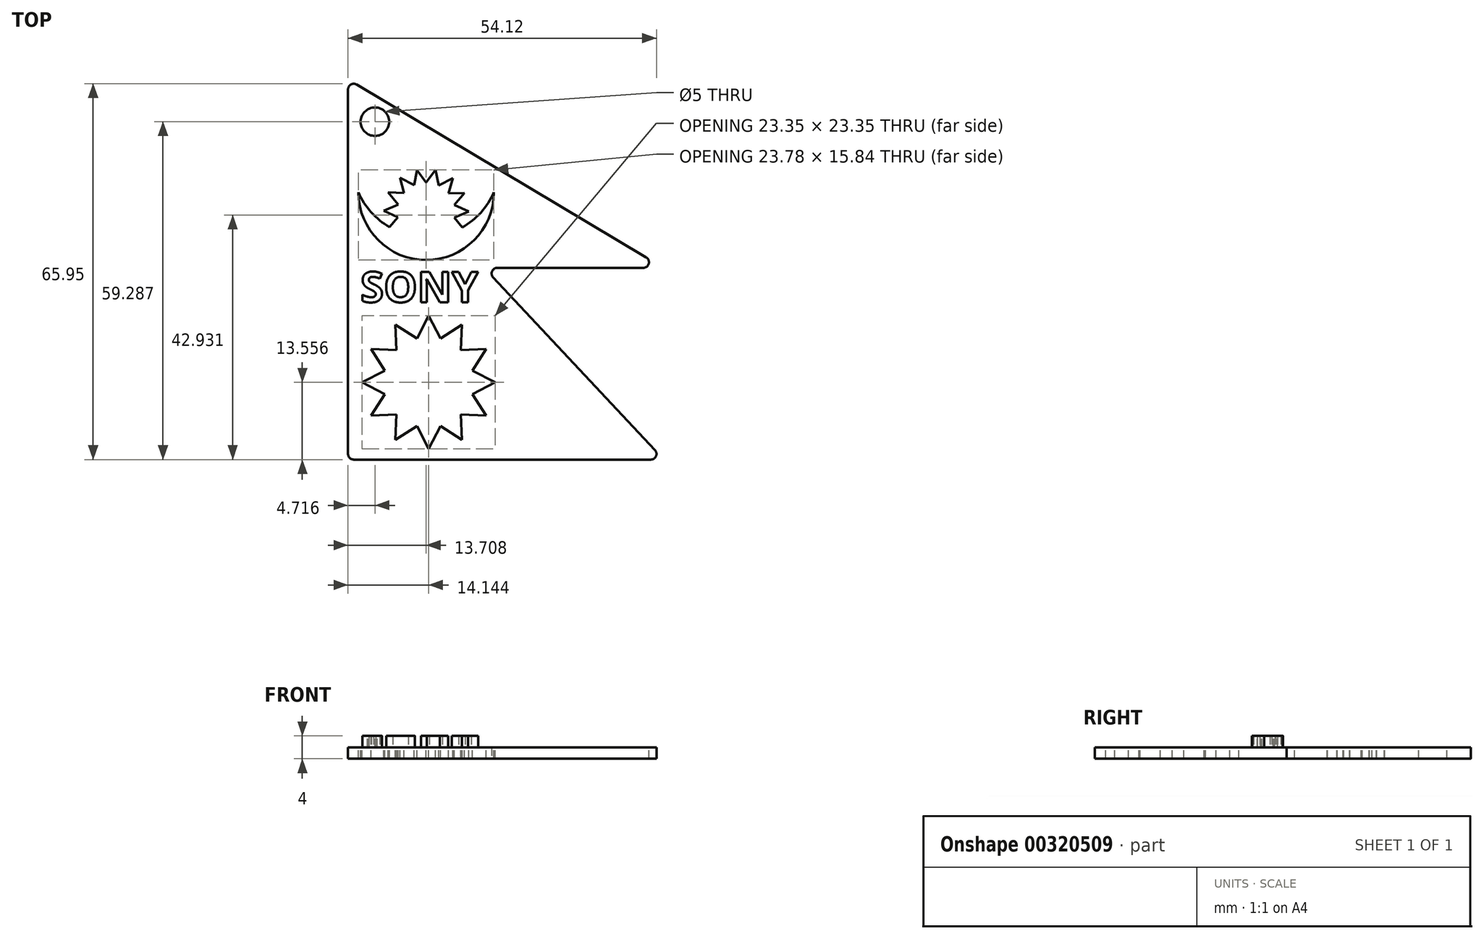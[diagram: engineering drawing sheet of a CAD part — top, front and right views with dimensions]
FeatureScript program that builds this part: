
annotation { "Feature Type Name" : "Feature", "Feature Type Description" : "" }
export const myFeature = defineFeature(function(context is Context, id is Id, definition is map)
    precondition{}
    {
        {
            var Q0;
            Q0=qCreatedBy(makeId("Top.planeOp"),FACE);
            var sketch = newSketch(context, id + "F0", { "sketchPlane" : qUnion([Q0])});
            skLineSegment(sketch, "E0", {"start": v(0, 66.7) * mm, "end": v(0, 0) * mm});
            skLineSegment(sketch, "E1", {"start": v(0, 66.7) * mm, "end": v(55.43, 33.64) * mm});
            skLineSegment(sketch, "E2", {"start": v(55.43, 33.64) * mm, "end": v(23.9, 33.64) * mm});
            skLineSegment(sketch, "E3", {"start": v(23.9, 33.64) * mm, "end": v(55.43, 0) * mm});
            skLineSegment(sketch, "E4", {"start": v(55.43, 0) * mm, "end": v(0, 0) * mm});
            skLineSegment(sketch, "E5", {"start": v(14.14, 25.23) * mm, "end": v(12.08, 21.25) * mm});
            skLineSegment(sketch, "E6.MirrorCS", {"start": v(14.14, 25.23) * mm, "end": v(16.2, 21.25) * mm});
            skLineSegment(sketch, "E7.1.0", {"start": v(19.98, 23.67) * mm, "end": v(19.78, 19.19) * mm});
            skLineSegment(sketch, "E7.1.1", {"start": v(19.98, 23.67) * mm, "end": v(16.2, 21.25) * mm});
            skLineSegment(sketch, "E7.2.0", {"start": v(24.25, 19.4) * mm, "end": v(21.84, 15.62) * mm});
            skLineSegment(sketch, "E7.2.1", {"start": v(24.25, 19.4) * mm, "end": v(19.78, 19.19) * mm});
            skLineSegment(sketch, "E7.3.0", {"start": v(25.82, 13.56) * mm, "end": v(21.84, 11.5) * mm});
            skLineSegment(sketch, "E7.3.1", {"start": v(25.82, 13.56) * mm, "end": v(21.84, 15.62) * mm});
            skLineSegment(sketch, "E7.4.0", {"start": v(24.25, 7.72) * mm, "end": v(19.78, 7.92) * mm});
            skLineSegment(sketch, "E7.4.1", {"start": v(24.25, 7.72) * mm, "end": v(21.84, 11.5) * mm});
            skLineSegment(sketch, "E7.5.0", {"start": v(19.98, 3.45) * mm, "end": v(16.2, 5.86) * mm});
            skLineSegment(sketch, "E7.5.1", {"start": v(19.98, 3.45) * mm, "end": v(19.78, 7.92) * mm});
            skLineSegment(sketch, "E7.6.0", {"start": v(14.14, 1.88) * mm, "end": v(12.08, 5.86) * mm});
            skLineSegment(sketch, "E7.6.1", {"start": v(14.14, 1.88) * mm, "end": v(16.2, 5.86) * mm});
            skLineSegment(sketch, "E7.7.0", {"start": v(8.3, 3.45) * mm, "end": v(8.51, 7.92) * mm});
            skLineSegment(sketch, "E7.7.1", {"start": v(8.3, 3.45) * mm, "end": v(12.08, 5.86) * mm});
            skLineSegment(sketch, "E7.8.0", {"start": v(4.03, 7.72) * mm, "end": v(6.45, 11.5) * mm});
            skLineSegment(sketch, "E7.8.1", {"start": v(4.03, 7.72) * mm, "end": v(8.51, 7.92) * mm});
            skLineSegment(sketch, "E7.9.0", {"start": v(2.47, 13.56) * mm, "end": v(6.45, 15.62) * mm});
            skLineSegment(sketch, "E7.9.1", {"start": v(2.47, 13.56) * mm, "end": v(6.45, 11.5) * mm});
            skLineSegment(sketch, "E7.10.0", {"start": v(4.03, 19.4) * mm, "end": v(8.51, 19.19) * mm});
            skLineSegment(sketch, "E7.10.1", {"start": v(4.03, 19.4) * mm, "end": v(6.45, 15.62) * mm});
            skLineSegment(sketch, "E7.11.0", {"start": v(8.3, 23.67) * mm, "end": v(12.08, 21.25) * mm});
            skLineSegment(sketch, "E7.11.1", {"start": v(8.3, 23.67) * mm, "end": v(8.51, 19.19) * mm});
            skSolve(sketch);
        }
        {
            var Q0;
            Q0=makeQuery(id+"F0.imprint","IMPRINT",FACE,{"disambiguationData":[TD([[makeQuery(id+"F0.imprint","IMPRINT",EDGE,{"derivedFrom":sQuery(id+"F0.wireOp",EDGE,"E0")}),1.0]])]});
            var sketch = newSketch(context, id + "F1", { "sketchPlane" : qUnion([Q0])});
            skArc(sketch, "E8", {"start": v(1.82, 46.9) * mm, "mid": v(13.7, 35.01) * mm, "end": v(25.6, 46.9) * mm});
            skArc(sketch, "E9", {"start": v(1.82, 46.9) * mm, "mid": v(4.06, 43.4) * mm, "end": v(7.29, 40.79) * mm});
            skLineSegment(sketch, "E10", {"start": v(13.7, 48.63) * mm, "end": v(12.12, 50.75) * mm});
            skLineSegment(sketch, "E11.MirrorCS", {"start": v(13.7, 48.63) * mm, "end": v(15.37, 50.85) * mm});
            skLineSegment(sketch, "E12.1.0", {"start": v(15.9, 48.13) * mm, "end": v(15.37, 50.85) * mm});
            skLineSegment(sketch, "E12.1.1", {"start": v(15.9, 48.13) * mm, "end": v(18.37, 49.4) * mm});
            skLineSegment(sketch, "E12.2.0", {"start": v(17.66, 46.72) * mm, "end": v(18.37, 49.4) * mm});
            skLineSegment(sketch, "E12.2.1", {"start": v(17.66, 46.72) * mm, "end": v(20.43, 46.8) * mm});
            skLineSegment(sketch, "E12.3.0", {"start": v(18.64, 44.7) * mm, "end": v(20.43, 46.8) * mm});
            skLineSegment(sketch, "E12.3.1", {"start": v(18.64, 44.7) * mm, "end": v(21.17, 43.56) * mm});
            skLineSegment(sketch, "E12.4.0", {"start": v(18.63, 42.44) * mm, "end": v(21.17, 43.56) * mm});
            skLineSegment(sketch, "E12.4.1", {"start": v(18.63, 42.44) * mm, "end": v(20.05, 40.75) * mm});
            skLineSegment(sketch, "E12.10.0", {"start": v(8.77, 42.5) * mm, "end": v(7.29, 40.79) * mm});
            skLineSegment(sketch, "E12.10.1", {"start": v(8.77, 42.5) * mm, "end": v(6.25, 43.66) * mm});
            skLineSegment(sketch, "E12.11.0", {"start": v(8.8, 44.76) * mm, "end": v(6.25, 43.66) * mm});
            skLineSegment(sketch, "E12.11.1", {"start": v(8.8, 44.76) * mm, "end": v(7.02, 46.9) * mm});
            skLineSegment(sketch, "E12.12.0", {"start": v(9.8, 46.78) * mm, "end": v(7.02, 46.9) * mm});
            skLineSegment(sketch, "E12.12.1", {"start": v(9.8, 46.78) * mm, "end": v(9.13, 49.47) * mm});
            skLineSegment(sketch, "E12.13.0", {"start": v(11.57, 48.16) * mm, "end": v(9.13, 49.47) * mm});
            skLineSegment(sketch, "E12.13.1", {"start": v(11.57, 48.16) * mm, "end": v(12.12, 50.75) * mm});
            skArc(sketch, "E13.trimOffspring", {"start": v(20.05, 40.75) * mm, "mid": v(23.33, 43.37) * mm, "end": v(25.6, 46.9) * mm});
            skSolve(sketch);
        }
        {
            var Q0;
            Q0=makeQuery(id+"F0.imprint","IMPRINT",FACE,{"disambiguationData":[TD([[makeQuery(id+"F0.imprint","IMPRINT",EDGE,{"derivedFrom":sQuery(id+"F0.wireOp",EDGE,"E0")}),1.0]])]});
            extrude(context, id + "F2", {"entities" : qUnion([Q0]), "oppositeDirection" : true, "depth" : 2 * mm});
        }
        {
            var Q0;
            Q0=makeQuery(id+"F1.imprint","IMPRINT",FACE,{"disambiguationData":[TD([[makeQuery(id+"F1.imprint","IMPRINT",EDGE,{"derivedFrom":sQuery(id+"F1.wireOp",EDGE,"E8")}),1.0]])]});
            extrude(context, id + "F3", {"entities" : qUnion([Q0]), "operationType" : NewBodyOperationType.REMOVE, "oppositeDirection" : true, "depth" : 25 * mm});
        }
        {
            var Q0;
            Q0=makeQuery(id+"F2.opExtrude","SWEPT_EDGE",EDGE,{"disambiguationData":[OSD([sQuery(id+"F0.wireOp",EDGE,"E0"),sQuery(id+"F0.wireOp",EDGE,"E4")])]});
            var Q1;
            Q1=makeQuery(id+"F2.opExtrude","SWEPT_EDGE",EDGE,{"disambiguationData":[OSD([sQuery(id+"F0.wireOp",EDGE,"E3"),sQuery(id+"F0.wireOp",EDGE,"E4")])]});
            var Q2;
            Q2=makeQuery(id+"F2.opExtrude","SWEPT_EDGE",EDGE,{"disambiguationData":[OSD([sQuery(id+"F0.wireOp",EDGE,"E2"),sQuery(id+"F0.wireOp",EDGE,"E3")])]});
            var Q3;
            Q3=makeQuery(id+"F2.opExtrude","SWEPT_EDGE",EDGE,{"disambiguationData":[OSD([sQuery(id+"F0.wireOp",EDGE,"E1"),sQuery(id+"F0.wireOp",EDGE,"E2")])]});
            var Q4;
            Q4=makeQuery(id+"F2.opExtrude","SWEPT_EDGE",EDGE,{"disambiguationData":[OSD([sQuery(id+"F0.wireOp",EDGE,"E0"),sQuery(id+"F0.wireOp",EDGE,"E1")])]});
            fillet(context, id + "F4", {"entities" : qUnion([Q0, Q1, Q2, Q3, Q4]), "radius" : 1 * mm, "tangentPropagation" : true, "allowEdgeOverflow" : false});
        }
        {
            var Q0;
            Q0=makeQuery(id+"F2.opExtrude","CAP_FACE",FACE,{"disambiguationData":[OSD([sQuery(id+"F0.wireOp",EDGE,"E0"),sQuery(id+"F0.wireOp",EDGE,"E1"),sQuery(id+"F0.wireOp",EDGE,"E2"),sQuery(id+"F0.wireOp",EDGE,"E3"),sQuery(id+"F0.wireOp",EDGE,"E4"),sQuery(id+"F0.wireOp",EDGE,"E5"),sQuery(id+"F0.wireOp",EDGE,"E6.MirrorCS"),sQuery(id+"F0.wireOp",EDGE,"E7.1.0"),sQuery(id+"F0.wireOp",EDGE,"E7.1.1"),sQuery(id+"F0.wireOp",EDGE,"E7.2.0"),sQuery(id+"F0.wireOp",EDGE,"E7.2.1"),sQuery(id+"F0.wireOp",EDGE,"E7.3.0"),sQuery(id+"F0.wireOp",EDGE,"E7.3.1"),sQuery(id+"F0.wireOp",EDGE,"E7.4.0"),sQuery(id+"F0.wireOp",EDGE,"E7.4.1"),sQuery(id+"F0.wireOp",EDGE,"E7.5.0"),sQuery(id+"F0.wireOp",EDGE,"E7.5.1"),sQuery(id+"F0.wireOp",EDGE,"E7.6.0"),sQuery(id+"F0.wireOp",EDGE,"E7.6.1"),sQuery(id+"F0.wireOp",EDGE,"E7.7.0"),sQuery(id+"F0.wireOp",EDGE,"E7.7.1"),sQuery(id+"F0.wireOp",EDGE,"E7.8.0"),sQuery(id+"F0.wireOp",EDGE,"E7.8.1"),sQuery(id+"F0.wireOp",EDGE,"E7.9.0"),sQuery(id+"F0.wireOp",EDGE,"E7.9.1"),sQuery(id+"F0.wireOp",EDGE,"E7.10.0"),sQuery(id+"F0.wireOp",EDGE,"E7.10.1"),sQuery(id+"F0.wireOp",EDGE,"E7.11.0"),sQuery(id+"F0.wireOp",EDGE,"E7.11.1")])],"isStart":true});
            var sketch = newSketch(context, id + "F5", { "sketchPlane" : qUnion([Q0])});
            skText(sketch, "E14", { "text": "SONY", "fontName": "OpenSans-Bold.ttf"});
            skPoint(sketch, "E14.firstSnap0", {"position": v(0, 32.97) * mm});
            const initialGuessF5  = {"E14": [0.00216, 0.02762, 1, 0, 0.00535]};
            skSetInitialGuess(sketch, initialGuessF5);
            skSolve(sketch);
        }
        {
            var Q0;
            Q0 = qSketchRegion(id + "F5", true);
            extrude(context, id + "F6", {"entities" : qUnion([Q0]), "operationType" : NewBodyOperationType.ADD, "depth" : 2 * mm});
        }
        {
            var Q0;
            {var subQ0=sQuery(id+"F0.wireOp",EDGE,"E4");var subQ1=sQuery(id+"F0.wireOp",EDGE,"E3");var subQ2=sQuery(id+"F0.wireOp",EDGE,"E7.7.1");var subQ3=sQuery(id+"F0.wireOp",EDGE,"E0");var subQ4=sQuery(id+"F0.wireOp",EDGE,"E7.10.1");var subQ5=sQuery(id+"F0.wireOp",EDGE,"E2");var subQ6=sQuery(id+"F0.wireOp",EDGE,"E7.11.1");var subQ7=sQuery(id+"F0.wireOp",EDGE,"E7.7.0");var subQ8=sQuery(id+"F0.wireOp",EDGE,"E1");var subQ9=sQuery(id+"F0.wireOp",EDGE,"E7.10.0");var subQ10=sQuery(id+"F0.wireOp",EDGE,"E7.3.0");var subQ11=sQuery(id+"F0.wireOp",EDGE,"E7.6.0");var subQ12=sQuery(id+"F0.wireOp",EDGE,"E7.2.1");var subQ13=sQuery(id+"F0.wireOp",EDGE,"E7.5.1");var subQ14=sQuery(id+"F0.wireOp",EDGE,"E7.3.1");var subQ15=sQuery(id+"F0.wireOp",EDGE,"E7.6.1");var subQ16=sQuery(id+"F0.wireOp",EDGE,"E7.11.0");var subQ17=sQuery(id+"F0.wireOp",EDGE,"E7.8.0");var subQ18=sQuery(id+"F0.wireOp",EDGE,"E7.2.0");var subQ19=sQuery(id+"F0.wireOp",EDGE,"E7.9.1");var subQ20=sQuery(id+"F0.wireOp",EDGE,"E7.4.0");var subQ21=sQuery(id+"F0.wireOp",EDGE,"E5");var subQ22=sQuery(id+"F0.wireOp",EDGE,"E7.4.1");var subQ23=sQuery(id+"F0.wireOp",EDGE,"E6.MirrorCS");var subQ24=sQuery(id+"F0.wireOp",EDGE,"E7.5.0");var subQ25=sQuery(id+"F0.wireOp",EDGE,"E7.1.0");var subQ26=sQuery(id+"F0.wireOp",EDGE,"E7.8.1");var subQ27=sQuery(id+"F0.wireOp",EDGE,"E7.1.1");var subQ28=sQuery(id+"F0.wireOp",EDGE,"E7.9.0");Q0=makeQuery(id+"F6.boolean.opBoolean","SPLIT",FACE,{"disambiguationData":[TD([makeQuery(id+"F2.opExtrude","SWEPT_FACE",FACE,{"disambiguationData":[OSD([subQ3])]})])],"derivedFrom":makeQuery(id+"F2.opExtrude","CAP_FACE",FACE,{"disambiguationData":[OSD([subQ3,subQ8,subQ5,subQ1,subQ0,subQ21,subQ23,subQ25,subQ27,subQ18,subQ12,subQ10,subQ14,subQ20,subQ22,subQ24,subQ13,subQ11,subQ15,subQ7,subQ2,subQ17,subQ26,subQ28,subQ19,subQ9,subQ4,subQ16,subQ6])],"isStart":true})});}
            var sketch = newSketch(context, id + "F7", { "sketchPlane" : qUnion([Q0])});
            skCircle(sketch, "E15", {"center": v(4.72, 59.29) * mm, "radius": 2.5 * mm});
            skSolve(sketch);
        }
        {
            var Q0;
            Q0=makeQuery(id+"F7.imprint","IMPRINT",FACE,{"disambiguationData":[TD([[makeQuery(id+"F7.imprint","IMPRINT",EDGE,{"derivedFrom":sQuery(id+"F7.wireOp",EDGE,"E15")}),1.0]])]});
            extrude(context, id + "F8", {"entities" : qUnion([Q0]), "operationType" : NewBodyOperationType.REMOVE, "oppositeDirection" : true, "depth" : 25 * mm});
        }
    });
